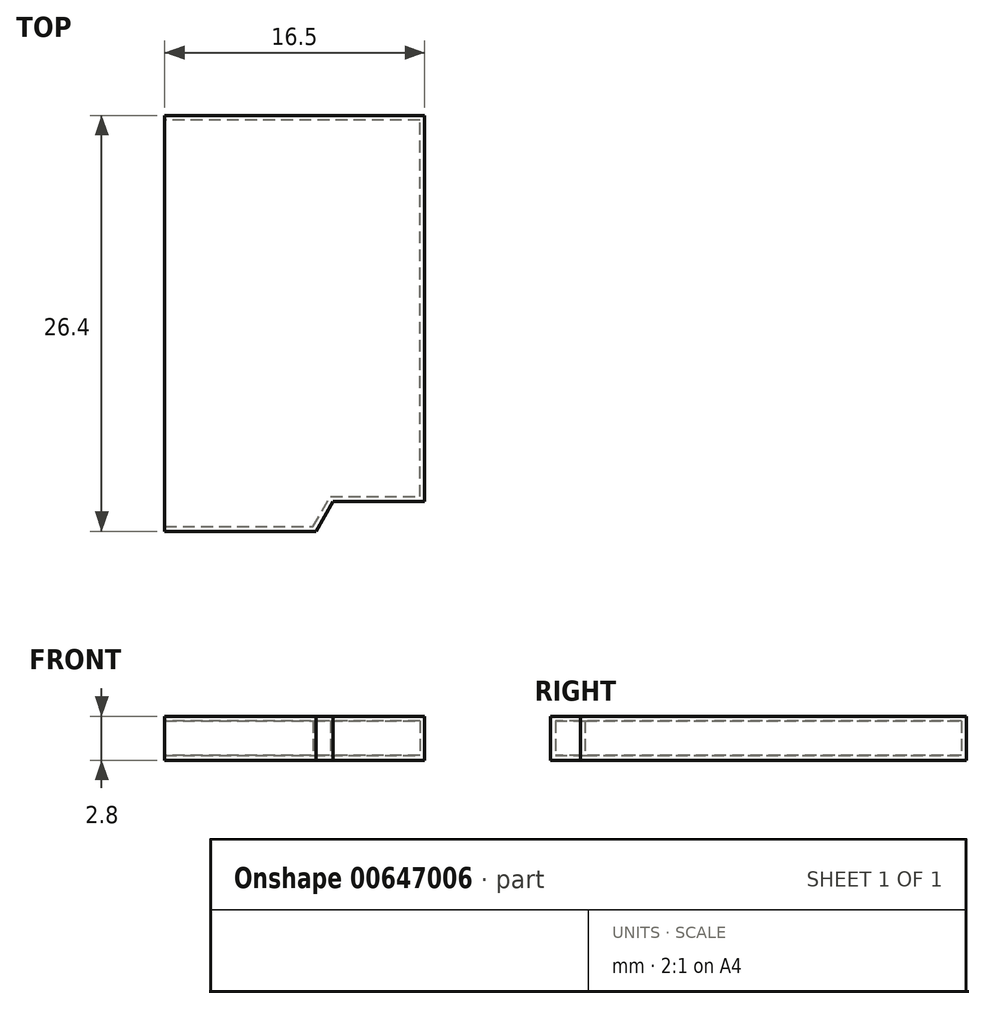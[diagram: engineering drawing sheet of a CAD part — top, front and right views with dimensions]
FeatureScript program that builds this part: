
annotation { "Feature Type Name" : "Feature", "Feature Type Description" : "" }
export const myFeature = defineFeature(function(context is Context, id is Id, definition is map)
    precondition{}
    {
        {
            var Q0;
            Q0=qCreatedBy(makeId("Top.planeOp"),FACE);
            var sketch = newSketch(context, id + "F0", { "sketchPlane" : qUnion([Q0])});
            skLineSegment(sketch, "E0", {"start": v(16.5, 1.9) * mm, "end": v(16.5, 26.4) * mm});
            skLineSegment(sketch, "E1", {"start": v(16.5, 26.4) * mm, "end": v(0, 26.4) * mm});
            skLineSegment(sketch, "E2", {"start": v(0, 26.4) * mm, "end": v(0, 0) * mm});
            skLineSegment(sketch, "E3", {"start": v(0, 0) * mm, "end": v(9.6, 0) * mm});
            skLineSegment(sketch, "E4", {"start": v(9.6, 0) * mm, "end": v(10.7, 1.9) * mm});
            skLineSegment(sketch, "E5", {"start": v(10.7, 1.9) * mm, "end": v(16.5, 1.9) * mm});
            skSolve(sketch);
        }
        {
            var Q0;
            Q0 = qSketchRegion(id + "F0", true);
            extrude(context, id + "F1", {"entities" : qUnion([Q0]), "depth" : 2.8 * mm, "offsetDistance" : 25 * mm});
        }
        {
            var Q0;
            Q0=makeQuery(id+"F1.opExtrude","SWEPT_FACE",FACE,{"disambiguationData":[OSD([sQuery(id+"F0.wireOp",EDGE,"E2")])]});
            shell(context, id + "F2", {"entities" : qUnion([Q0]), "thickness" : 0.3 * mm});
        }
    });
